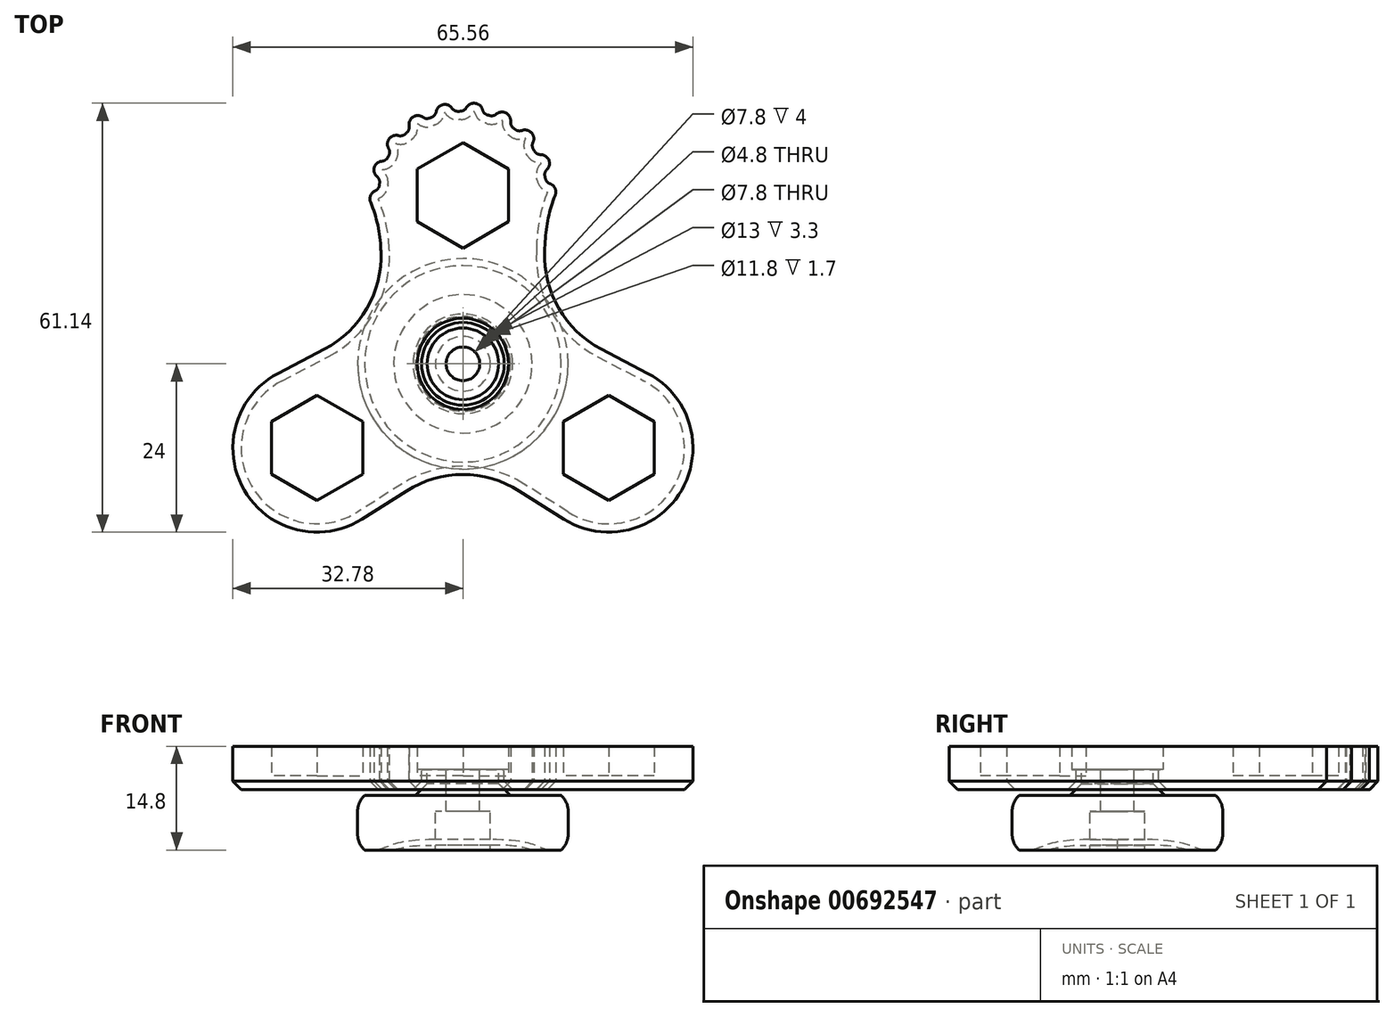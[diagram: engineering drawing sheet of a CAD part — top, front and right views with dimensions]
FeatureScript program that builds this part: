
annotation { "Feature Type Name" : "Feature", "Feature Type Description" : "" }
export const myFeature = defineFeature(function(context is Context, id is Id, definition is map)
    precondition{}
    {
        {
            var Q0;
            Q0=qCreatedBy(makeId("Top.planeOp"),FACE);
            var sketch = newSketch(context, id + "F0", { "sketchPlane" : qUnion([Q0])});
            skCircle(sketch, "E0", {"center": v(0, 0) * mm, "radius": 6.5 * mm});
            skCircle(sketch, "E1.cCircle", {"center": v(0, 24) * mm, "radius": 6.5 * mm, "construction": true});
            skLineSegment(sketch, "E1.0", {"start": v(6.5, 27.75) * mm, "end": v(6.5, 20.25) * mm});
            skLineSegment(sketch, "E1.1", {"start": v(6.5, 20.25) * mm, "end": v(0, 16.5) * mm});
            skLineSegment(sketch, "E1.2", {"start": v(0, 16.5) * mm, "end": v(-6.5, 20.25) * mm});
            skLineSegment(sketch, "E1.3", {"start": v(-6.5, 20.25) * mm, "end": v(-6.5, 27.75) * mm});
            skLineSegment(sketch, "E1.4", {"start": v(-6.5, 27.75) * mm, "end": v(0, 31.5) * mm});
            skLineSegment(sketch, "E1.5", {"start": v(0, 31.5) * mm, "end": v(6.5, 27.75) * mm});
            skPoint(sketch, "E1.0.midPoint", {"position": v(6.5, 24) * mm});
            skCircle(sketch, "E2", {"center": v(0, 24) * mm, "radius": 12 * mm});
            skCircle(sketch, "E3", {"center": v(0, 0) * mm, "radius": 11 * mm});
            skLineSegment(sketch, "E4", {"start": v(-11.99, 23.5) * mm, "end": v(-11, -0.46) * mm});
            skLineSegment(sketch, "E5", {"start": v(11.99, 23.5) * mm, "end": v(11, -0.46) * mm});
            skCircle(sketch, "E6.1.0", {"center": v(-20.78, -12) * mm, "radius": 12 * mm});
            skLineSegment(sketch, "E6.1.1", {"start": v(-27.28, -15.75) * mm, "end": v(-27.28, -8.25) * mm});
            skLineSegment(sketch, "E6.1.2", {"start": v(-27.28, -8.25) * mm, "end": v(-20.78, -4.5) * mm});
            skLineSegment(sketch, "E6.1.3", {"start": v(-20.78, -4.5) * mm, "end": v(-14.28, -8.25) * mm});
            skLineSegment(sketch, "E6.1.4", {"start": v(-14.28, -8.25) * mm, "end": v(-14.28, -15.75) * mm});
            skLineSegment(sketch, "E6.1.5", {"start": v(-14.28, -15.75) * mm, "end": v(-20.78, -19.5) * mm});
            skLineSegment(sketch, "E6.1.6", {"start": v(-20.78, -19.5) * mm, "end": v(-27.28, -15.75) * mm});
            skLineSegment(sketch, "E6.1.7", {"start": v(-14.36, -22.13) * mm, "end": v(5.9, -9.29) * mm});
            skLineSegment(sketch, "E6.1.8", {"start": v(-26.35, -1.37) * mm, "end": v(-5.1, 9.75) * mm});
            skCircle(sketch, "E6.2.0", {"center": v(20.78, -12) * mm, "radius": 12 * mm});
            skLineSegment(sketch, "E6.2.1", {"start": v(27.28, -15.75) * mm, "end": v(20.78, -19.5) * mm});
            skLineSegment(sketch, "E6.2.2", {"start": v(20.78, -19.5) * mm, "end": v(14.28, -15.75) * mm});
            skLineSegment(sketch, "E6.2.3", {"start": v(14.28, -15.75) * mm, "end": v(14.28, -8.25) * mm});
            skLineSegment(sketch, "E6.2.4", {"start": v(14.28, -8.25) * mm, "end": v(20.78, -4.5) * mm});
            skLineSegment(sketch, "E6.2.5", {"start": v(20.78, -4.5) * mm, "end": v(27.28, -8.25) * mm});
            skLineSegment(sketch, "E6.2.6", {"start": v(27.28, -8.25) * mm, "end": v(27.28, -15.75) * mm});
            skLineSegment(sketch, "E6.2.7", {"start": v(26.35, -1.37) * mm, "end": v(5.1, 9.75) * mm});
            skLineSegment(sketch, "E6.2.8", {"start": v(14.36, -22.13) * mm, "end": v(-5.9, -9.29) * mm});
            skSolve(sketch);
        }
        {
            var Q0;
            Q0 = qSketchRegion(id + "F0", true);
            var Q1;
            Q1=makeQuery(id+"F0.imprint","IMPRINT",FACE,{"disambiguationData":[TD([[makeQuery(id+"F0.imprint","IMPRINT",EDGE,{"derivedFrom":sQuery(id+"F0.wireOp",EDGE,"E0")}),-1.0]])]});
            extrude(context, id + "F1", {"entities" : qUnion([Q0, Q1]), "depth" : 4.2 * mm, "offsetDistance" : 25 * mm});
        }
        {
            var Q0;
            Q0=makeQuery(id+"F1.opExtrude","CAP_FACE",FACE,{"disambiguationData":[OSD([sQuery(id+"F0.wireOp",EDGE,"E0"),sQuery(id+"F0.wireOp",EDGE,"E1.0"),sQuery(id+"F0.wireOp",EDGE,"E1.1"),sQuery(id+"F0.wireOp",EDGE,"E1.2"),sQuery(id+"F0.wireOp",EDGE,"E1.3"),sQuery(id+"F0.wireOp",EDGE,"E1.4"),sQuery(id+"F0.wireOp",EDGE,"E1.5"),sQuery(id+"F0.wireOp",EDGE,"E2"),sQuery(id+"F0.wireOp",EDGE,"E4"),sQuery(id+"F0.wireOp",EDGE,"E5"),sQuery(id+"F0.wireOp",EDGE,"E6.1.0"),sQuery(id+"F0.wireOp",EDGE,"E6.1.1"),sQuery(id+"F0.wireOp",EDGE,"E6.1.2"),sQuery(id+"F0.wireOp",EDGE,"E6.1.3"),sQuery(id+"F0.wireOp",EDGE,"E6.1.4"),sQuery(id+"F0.wireOp",EDGE,"E6.1.5"),sQuery(id+"F0.wireOp",EDGE,"E6.1.6"),sQuery(id+"F0.wireOp",EDGE,"E6.1.7"),sQuery(id+"F0.wireOp",EDGE,"E6.1.8"),sQuery(id+"F0.wireOp",EDGE,"E6.2.0"),sQuery(id+"F0.wireOp",EDGE,"E6.2.1"),sQuery(id+"F0.wireOp",EDGE,"E6.2.2"),sQuery(id+"F0.wireOp",EDGE,"E6.2.3"),sQuery(id+"F0.wireOp",EDGE,"E6.2.4"),sQuery(id+"F0.wireOp",EDGE,"E6.2.5"),sQuery(id+"F0.wireOp",EDGE,"E6.2.6"),sQuery(id+"F0.wireOp",EDGE,"E6.2.7"),sQuery(id+"F0.wireOp",EDGE,"E6.2.8")])],"isStart":true});
            var sketch = newSketch(context, id + "F2", { "sketchPlane" : qUnion([Q0])});
            skCircle(sketch, "E7", {"center": v(0, 0) * mm, "radius": 5.9 * mm});
            skSolve(sketch);
        }
        {
            var Q0;
            Q0=makeQuery(id+"F2.imprint","IMPRINT",FACE,{"disambiguationData":[TD([[makeQuery(id+"F2.imprint","IMPRINT",EDGE,{"derivedFrom":makeQuery(id+"F1.opExtrude","CAP_EDGE",EDGE,{"disambiguationData":[OSD([sQuery(id+"F0.wireOp",EDGE,"E1.0")])],"isStart":true})}),1.0]])]});
            var Q1;
            Q1=makeQuery(id+"F2.imprint","IMPRINT",FACE,{"disambiguationData":[TD([[makeQuery(id+"F2.imprint","IMPRINT",EDGE,{"derivedFrom":makeQuery(id+"F1.opExtrude","CAP_EDGE",EDGE,{"disambiguationData":[OSD([sQuery(id+"F0.wireOp",EDGE,"E0")])],"isStart":true})}),1.0]])]});
            var Q2;
            Q2=makeQuery(id+"F2.imprint","IMPRINT",FACE,{"disambiguationData":[TD([[makeQuery(id+"F2.imprint","IMPRINT",EDGE,{"derivedFrom":makeQuery(id+"F1.opExtrude","CAP_EDGE",EDGE,{"disambiguationData":[OSD([sQuery(id+"F0.wireOp",EDGE,"E0")])],"isStart":true})}),-1.0]])]});
            var Q3;
            Q3=makeQuery(id+"F2.imprint","IMPRINT",FACE,{"disambiguationData":[TD([[makeQuery(id+"F2.imprint","IMPRINT",EDGE,{"derivedFrom":makeQuery(id+"F1.opExtrude","CAP_EDGE",EDGE,{"disambiguationData":[OSD([sQuery(id+"F0.wireOp",EDGE,"E6.2.1")])],"isStart":true})}),1.0]])]});
            var Q4;
            Q4=makeQuery(id+"F2.imprint","IMPRINT",FACE,{"disambiguationData":[TD([[makeQuery(id+"F2.imprint","IMPRINT",EDGE,{"derivedFrom":makeQuery(id+"F1.opExtrude","CAP_EDGE",EDGE,{"disambiguationData":[OSD([sQuery(id+"F0.wireOp",EDGE,"E6.1.1")])],"isStart":true})}),1.0]])]});
            extrude(context, id + "F3", {"entities" : qUnion([Q0, Q1, Q2, Q3, Q4]), "operationType" : NewBodyOperationType.ADD, "depth" : 2 * mm, "offsetDistance" : 25 * mm});
        }
        {
            var Q0;
            {var subQ0=sQuery(id+"F2.wireOp",EDGE,"E7");Q0=makeQuery(id+"F3.boolean.opBoolean","SPLIT",FACE,{"disambiguationData":[TD([makeQuery(id+"F1.opExtrude","SWEPT_FACE",FACE,{"disambiguationData":[OSD([sQuery(id+"F0.wireOp",EDGE,"E0")])]})])],"derivedFrom":makeQuery(id+"F3.opExtrude","CAP_FACE",FACE,{"disambiguationData":[OSD([sQuery(id+"F0.wireOp",EDGE,"E2"),sQuery(id+"F0.wireOp",EDGE,"E4"),sQuery(id+"F0.wireOp",EDGE,"E5"),sQuery(id+"F0.wireOp",EDGE,"E6.1.0"),sQuery(id+"F0.wireOp",EDGE,"E6.1.7"),sQuery(id+"F0.wireOp",EDGE,"E6.1.8"),sQuery(id+"F0.wireOp",EDGE,"E6.2.0"),sQuery(id+"F0.wireOp",EDGE,"E6.2.7"),sQuery(id+"F0.wireOp",EDGE,"E6.2.8"),subQ0])],"isStart":true})});}
            extrude(context, id + "F4", {"entities" : qUnion([Q0]), "operationType" : NewBodyOperationType.ADD, "depth" : .9 * mm, "offsetDistance" : 25 * mm});
        }
        {
            var Q0;
            {var subQ0=sQuery(id+"F0.wireOp",EDGE,"E6.1.8");var subQ1=sQuery(id+"F0.wireOp",EDGE,"E4");Q0=makeQuery(id+"F3.boolean.opBoolean","MERGE",EDGE,{"derivedFrom":[makeQuery(id+"F1.opExtrude","SWEPT_EDGE",EDGE,{"disambiguationData":[OSD([subQ1,subQ0])]}),makeQuery(id+"F3.opExtrude","SWEPT_EDGE",EDGE,{"disambiguationData":[OSD([subQ1,subQ0])]})]});}
            var Q1;
            {var subQ0=sQuery(id+"F0.wireOp",EDGE,"E6.2.7");var subQ1=sQuery(id+"F0.wireOp",EDGE,"E5");Q1=makeQuery(id+"F3.boolean.opBoolean","MERGE",EDGE,{"derivedFrom":[makeQuery(id+"F1.opExtrude","SWEPT_EDGE",EDGE,{"disambiguationData":[OSD([subQ1,subQ0])]}),makeQuery(id+"F3.opExtrude","SWEPT_EDGE",EDGE,{"disambiguationData":[OSD([subQ1,subQ0])]})]});}
            var Q2;
            {var subQ0=sQuery(id+"F0.wireOp",EDGE,"E6.2.8");var subQ1=sQuery(id+"F0.wireOp",EDGE,"E6.1.7");Q2=makeQuery(id+"F3.boolean.opBoolean","MERGE",EDGE,{"derivedFrom":[makeQuery(id+"F1.opExtrude","SWEPT_EDGE",EDGE,{"disambiguationData":[OSD([subQ1,subQ0])]}),makeQuery(id+"F3.opExtrude","SWEPT_EDGE",EDGE,{"disambiguationData":[OSD([subQ1,subQ0])]})]});}
            fillet(context, id + "F5", {"entities" : qUnion([Q0, Q1, Q2]), "radius" : 15 * mm, "tangentPropagation" : true, "allowEdgeOverflow" : false});
        }
        {
            var Q0;
            Q0=makeQuery(id+"F3.opExtrude","CAP_FACE",FACE,{"disambiguationData":[OSD([sQuery(id+"F0.wireOp",EDGE,"E2"),sQuery(id+"F0.wireOp",EDGE,"E4"),sQuery(id+"F0.wireOp",EDGE,"E5"),sQuery(id+"F0.wireOp",EDGE,"E6.1.0"),sQuery(id+"F0.wireOp",EDGE,"E6.1.7"),sQuery(id+"F0.wireOp",EDGE,"E6.1.8"),sQuery(id+"F0.wireOp",EDGE,"E6.2.0"),sQuery(id+"F0.wireOp",EDGE,"E6.2.7"),sQuery(id+"F0.wireOp",EDGE,"E6.2.8"),sQuery(id+"F2.wireOp",EDGE,"E7")])],"isStart":false});
            var sketch = newSketch(context, id + "F6", { "sketchPlane" : qUnion([Q0])});
            skCircle(sketch, "E8", {"center": v(-11.99, -23.5) * mm, "radius": 1.25 * mm});
            skCircle(sketch, "E9.1.0", {"center": v(-11.44, -27.63) * mm, "radius": 1.25 * mm});
            skCircle(sketch, "E9.2.0", {"center": v(-9.5, -31.32) * mm, "radius": 1.25 * mm});
            skCircle(sketch, "E9.3.0", {"center": v(-6.43, -34.13) * mm, "radius": 1.25 * mm});
            skCircle(sketch, "E9.4.0", {"center": v(-2.57, -35.72) * mm, "radius": 1.25 * mm});
            skCircle(sketch, "E9.5.0", {"center": v(1.59, -35.9) * mm, "radius": 1.25 * mm});
            skPoint(sketch, "E9.center", {"position": v(0, -24) * mm});
            skLineSegment(sketch, "E9.anchor1", {"start": v(0, -24) * mm, "end": v(-11.99, -23.5) * mm, "construction": true});
            skLineSegment(sketch, "E9.anchor2", {"start": v(0, -24) * mm, "end": v(11.99, -24.5) * mm, "construction": true});
            skCircle(sketch, "E10.1.6.0", {"center": v(5.56, -34.63) * mm, "radius": 1.25 * mm});
            skCircle(sketch, "E10.1.7.0", {"center": v(8.86, -32.09) * mm, "radius": 1.25 * mm});
            skCircle(sketch, "E10.1.8.0", {"center": v(11.1, -28.57) * mm, "radius": 1.25 * mm});
            skCircle(sketch, "E10.1.9.0", {"center": v(11.99, -24.5) * mm, "radius": 1.25 * mm});
            skSolve(sketch);
        }
        {
            var Q0;
            Q0 = qSketchRegion(id + "F6", true);
            var Q1;
            Q1=makeQuery(id+"F1.opExtrude","CAP_FACE",FACE,{"disambiguationData":[OSD([sQuery(id+"F0.wireOp",EDGE,"E0"),sQuery(id+"F0.wireOp",EDGE,"E1.0"),sQuery(id+"F0.wireOp",EDGE,"E1.1"),sQuery(id+"F0.wireOp",EDGE,"E1.2"),sQuery(id+"F0.wireOp",EDGE,"E1.3"),sQuery(id+"F0.wireOp",EDGE,"E1.4"),sQuery(id+"F0.wireOp",EDGE,"E1.5"),sQuery(id+"F0.wireOp",EDGE,"E2"),sQuery(id+"F0.wireOp",EDGE,"E4"),sQuery(id+"F0.wireOp",EDGE,"E5"),sQuery(id+"F0.wireOp",EDGE,"E6.1.0"),sQuery(id+"F0.wireOp",EDGE,"E6.1.1"),sQuery(id+"F0.wireOp",EDGE,"E6.1.2"),sQuery(id+"F0.wireOp",EDGE,"E6.1.3"),sQuery(id+"F0.wireOp",EDGE,"E6.1.4"),sQuery(id+"F0.wireOp",EDGE,"E6.1.5"),sQuery(id+"F0.wireOp",EDGE,"E6.1.6"),sQuery(id+"F0.wireOp",EDGE,"E6.1.7"),sQuery(id+"F0.wireOp",EDGE,"E6.1.8"),sQuery(id+"F0.wireOp",EDGE,"E6.2.0"),sQuery(id+"F0.wireOp",EDGE,"E6.2.1"),sQuery(id+"F0.wireOp",EDGE,"E6.2.2"),sQuery(id+"F0.wireOp",EDGE,"E6.2.3"),sQuery(id+"F0.wireOp",EDGE,"E6.2.4"),sQuery(id+"F0.wireOp",EDGE,"E6.2.5"),sQuery(id+"F0.wireOp",EDGE,"E6.2.6"),sQuery(id+"F0.wireOp",EDGE,"E6.2.7"),sQuery(id+"F0.wireOp",EDGE,"E6.2.8")])],"isStart":false});
            extrude(context, id + "F7", {"entities" : qUnion([Q0]), "operationType" : NewBodyOperationType.ADD, "endBound" : BoundingType.UP_TO_SURFACE, "oppositeDirection" : true, "depth" : 25 * mm, "endBoundEntityFace" : qUnion([Q1]), "offsetDistance" : 25 * mm});
        }
        {
            var Q0;
            {var subQ0=sQuery(id+"F0.wireOp",EDGE,"E2");Q0=makeQuery(id+"F7.boolean.opBoolean","INTERSECT",EDGE,{"disambiguationData":[OD(0.0)],"derivedFrom":[makeQuery(id+"F3.boolean.opBoolean","MERGE",FACE,{"derivedFrom":[makeQuery(id+"F1.opExtrude","SWEPT_FACE",FACE,{"disambiguationData":[OSD([subQ0])]}),makeQuery(id+"F3.opExtrude","SWEPT_FACE",FACE,{"disambiguationData":[OSD([subQ0])]})]}),makeQuery(id+"F7.opExtrude","SWEPT_FACE",FACE,{"disambiguationData":[OSD([sQuery(id+"F6.wireOp",EDGE,"E9.5.0")])]})]});}
            var Q1;
            {var subQ0=sQuery(id+"F0.wireOp",EDGE,"E2");Q1=makeQuery(id+"F7.boolean.opBoolean","INTERSECT",EDGE,{"disambiguationData":[OD(1.0)],"derivedFrom":[makeQuery(id+"F3.boolean.opBoolean","MERGE",FACE,{"derivedFrom":[makeQuery(id+"F1.opExtrude","SWEPT_FACE",FACE,{"disambiguationData":[OSD([subQ0])]}),makeQuery(id+"F3.opExtrude","SWEPT_FACE",FACE,{"disambiguationData":[OSD([subQ0])]})]}),makeQuery(id+"F7.opExtrude","SWEPT_FACE",FACE,{"disambiguationData":[OSD([sQuery(id+"F6.wireOp",EDGE,"E9.5.0")])]})]});}
            var Q2;
            {var subQ0=sQuery(id+"F0.wireOp",EDGE,"E2");Q2=makeQuery(id+"F7.boolean.opBoolean","INTERSECT",EDGE,{"derivedFrom":[makeQuery(id+"F3.boolean.opBoolean","MERGE",FACE,{"derivedFrom":[makeQuery(id+"F1.opExtrude","SWEPT_FACE",FACE,{"disambiguationData":[OSD([subQ0])]}),makeQuery(id+"F3.opExtrude","SWEPT_FACE",FACE,{"disambiguationData":[OSD([subQ0])]})]}),makeQuery(id+"F7.opExtrude","SWEPT_FACE",FACE,{"disambiguationData":[OSD([sQuery(id+"F6.wireOp",EDGE,"E8")])]})]});}
            var Q3;
            {var subQ0=sQuery(id+"F0.wireOp",EDGE,"E2");Q3=makeQuery(id+"F7.boolean.opBoolean","INTERSECT",EDGE,{"disambiguationData":[OD(0.0)],"derivedFrom":[makeQuery(id+"F3.boolean.opBoolean","MERGE",FACE,{"derivedFrom":[makeQuery(id+"F1.opExtrude","SWEPT_FACE",FACE,{"disambiguationData":[OSD([subQ0])]}),makeQuery(id+"F3.opExtrude","SWEPT_FACE",FACE,{"disambiguationData":[OSD([subQ0])]})]}),makeQuery(id+"F7.opExtrude","SWEPT_FACE",FACE,{"disambiguationData":[OSD([sQuery(id+"F6.wireOp",EDGE,"E9.1.0")])]})]});}
            var Q4;
            {var subQ0=sQuery(id+"F0.wireOp",EDGE,"E2");Q4=makeQuery(id+"F7.boolean.opBoolean","INTERSECT",EDGE,{"disambiguationData":[OD(1.0)],"derivedFrom":[makeQuery(id+"F3.boolean.opBoolean","MERGE",FACE,{"derivedFrom":[makeQuery(id+"F1.opExtrude","SWEPT_FACE",FACE,{"disambiguationData":[OSD([subQ0])]}),makeQuery(id+"F3.opExtrude","SWEPT_FACE",FACE,{"disambiguationData":[OSD([subQ0])]})]}),makeQuery(id+"F7.opExtrude","SWEPT_FACE",FACE,{"disambiguationData":[OSD([sQuery(id+"F6.wireOp",EDGE,"E9.1.0")])]})]});}
            var Q5;
            {var subQ0=sQuery(id+"F0.wireOp",EDGE,"E2");Q5=makeQuery(id+"F7.boolean.opBoolean","INTERSECT",EDGE,{"disambiguationData":[OD(0.0)],"derivedFrom":[makeQuery(id+"F3.boolean.opBoolean","MERGE",FACE,{"derivedFrom":[makeQuery(id+"F1.opExtrude","SWEPT_FACE",FACE,{"disambiguationData":[OSD([subQ0])]}),makeQuery(id+"F3.opExtrude","SWEPT_FACE",FACE,{"disambiguationData":[OSD([subQ0])]})]}),makeQuery(id+"F7.opExtrude","SWEPT_FACE",FACE,{"disambiguationData":[OSD([sQuery(id+"F6.wireOp",EDGE,"E9.2.0")])]})]});}
            var Q6;
            {var subQ0=sQuery(id+"F0.wireOp",EDGE,"E2");Q6=makeQuery(id+"F7.boolean.opBoolean","INTERSECT",EDGE,{"disambiguationData":[OD(1.0)],"derivedFrom":[makeQuery(id+"F3.boolean.opBoolean","MERGE",FACE,{"derivedFrom":[makeQuery(id+"F1.opExtrude","SWEPT_FACE",FACE,{"disambiguationData":[OSD([subQ0])]}),makeQuery(id+"F3.opExtrude","SWEPT_FACE",FACE,{"disambiguationData":[OSD([subQ0])]})]}),makeQuery(id+"F7.opExtrude","SWEPT_FACE",FACE,{"disambiguationData":[OSD([sQuery(id+"F6.wireOp",EDGE,"E9.2.0")])]})]});}
            var Q7;
            {var subQ0=sQuery(id+"F0.wireOp",EDGE,"E2");Q7=makeQuery(id+"F7.boolean.opBoolean","INTERSECT",EDGE,{"disambiguationData":[OD(0.0)],"derivedFrom":[makeQuery(id+"F3.boolean.opBoolean","MERGE",FACE,{"derivedFrom":[makeQuery(id+"F1.opExtrude","SWEPT_FACE",FACE,{"disambiguationData":[OSD([subQ0])]}),makeQuery(id+"F3.opExtrude","SWEPT_FACE",FACE,{"disambiguationData":[OSD([subQ0])]})]}),makeQuery(id+"F7.opExtrude","SWEPT_FACE",FACE,{"disambiguationData":[OSD([sQuery(id+"F6.wireOp",EDGE,"E9.3.0")])]})]});}
            var Q8;
            {var subQ0=sQuery(id+"F0.wireOp",EDGE,"E2");Q8=makeQuery(id+"F7.boolean.opBoolean","INTERSECT",EDGE,{"disambiguationData":[OD(1.0)],"derivedFrom":[makeQuery(id+"F3.boolean.opBoolean","MERGE",FACE,{"derivedFrom":[makeQuery(id+"F1.opExtrude","SWEPT_FACE",FACE,{"disambiguationData":[OSD([subQ0])]}),makeQuery(id+"F3.opExtrude","SWEPT_FACE",FACE,{"disambiguationData":[OSD([subQ0])]})]}),makeQuery(id+"F7.opExtrude","SWEPT_FACE",FACE,{"disambiguationData":[OSD([sQuery(id+"F6.wireOp",EDGE,"E9.3.0")])]})]});}
            var Q9;
            {var subQ0=sQuery(id+"F0.wireOp",EDGE,"E2");Q9=makeQuery(id+"F7.boolean.opBoolean","INTERSECT",EDGE,{"disambiguationData":[OD(0.0)],"derivedFrom":[makeQuery(id+"F3.boolean.opBoolean","MERGE",FACE,{"derivedFrom":[makeQuery(id+"F1.opExtrude","SWEPT_FACE",FACE,{"disambiguationData":[OSD([subQ0])]}),makeQuery(id+"F3.opExtrude","SWEPT_FACE",FACE,{"disambiguationData":[OSD([subQ0])]})]}),makeQuery(id+"F7.opExtrude","SWEPT_FACE",FACE,{"disambiguationData":[OSD([sQuery(id+"F6.wireOp",EDGE,"E9.4.0")])]})]});}
            var Q10;
            {var subQ0=sQuery(id+"F0.wireOp",EDGE,"E2");Q10=makeQuery(id+"F7.boolean.opBoolean","INTERSECT",EDGE,{"disambiguationData":[OD(1.0)],"derivedFrom":[makeQuery(id+"F3.boolean.opBoolean","MERGE",FACE,{"derivedFrom":[makeQuery(id+"F1.opExtrude","SWEPT_FACE",FACE,{"disambiguationData":[OSD([subQ0])]}),makeQuery(id+"F3.opExtrude","SWEPT_FACE",FACE,{"disambiguationData":[OSD([subQ0])]})]}),makeQuery(id+"F7.opExtrude","SWEPT_FACE",FACE,{"disambiguationData":[OSD([sQuery(id+"F6.wireOp",EDGE,"E9.4.0")])]})]});}
            var Q11;
            {var subQ0=sQuery(id+"F0.wireOp",EDGE,"E2");Q11=makeQuery(id+"F7.boolean.opBoolean","INTERSECT",EDGE,{"derivedFrom":[makeQuery(id+"F3.boolean.opBoolean","MERGE",FACE,{"derivedFrom":[makeQuery(id+"F1.opExtrude","SWEPT_FACE",FACE,{"disambiguationData":[OSD([subQ0])]}),makeQuery(id+"F3.opExtrude","SWEPT_FACE",FACE,{"disambiguationData":[OSD([subQ0])]})]}),makeQuery(id+"F7.opExtrude","SWEPT_FACE",FACE,{"disambiguationData":[OSD([sQuery(id+"F6.wireOp",EDGE,"E10.1.9.0")])]})]});}
            var Q12;
            {var subQ0=sQuery(id+"F0.wireOp",EDGE,"E2");Q12=makeQuery(id+"F7.boolean.opBoolean","INTERSECT",EDGE,{"disambiguationData":[OD(1.0)],"derivedFrom":[makeQuery(id+"F3.boolean.opBoolean","MERGE",FACE,{"derivedFrom":[makeQuery(id+"F1.opExtrude","SWEPT_FACE",FACE,{"disambiguationData":[OSD([subQ0])]}),makeQuery(id+"F3.opExtrude","SWEPT_FACE",FACE,{"disambiguationData":[OSD([subQ0])]})]}),makeQuery(id+"F7.opExtrude","SWEPT_FACE",FACE,{"disambiguationData":[OSD([sQuery(id+"F6.wireOp",EDGE,"E10.1.8.0")])]})]});}
            var Q13;
            {var subQ0=sQuery(id+"F0.wireOp",EDGE,"E2");Q13=makeQuery(id+"F7.boolean.opBoolean","INTERSECT",EDGE,{"disambiguationData":[OD(0.0)],"derivedFrom":[makeQuery(id+"F3.boolean.opBoolean","MERGE",FACE,{"derivedFrom":[makeQuery(id+"F1.opExtrude","SWEPT_FACE",FACE,{"disambiguationData":[OSD([subQ0])]}),makeQuery(id+"F3.opExtrude","SWEPT_FACE",FACE,{"disambiguationData":[OSD([subQ0])]})]}),makeQuery(id+"F7.opExtrude","SWEPT_FACE",FACE,{"disambiguationData":[OSD([sQuery(id+"F6.wireOp",EDGE,"E10.1.8.0")])]})]});}
            var Q14;
            {var subQ0=sQuery(id+"F0.wireOp",EDGE,"E2");Q14=makeQuery(id+"F7.boolean.opBoolean","INTERSECT",EDGE,{"disambiguationData":[OD(1.0)],"derivedFrom":[makeQuery(id+"F3.boolean.opBoolean","MERGE",FACE,{"derivedFrom":[makeQuery(id+"F1.opExtrude","SWEPT_FACE",FACE,{"disambiguationData":[OSD([subQ0])]}),makeQuery(id+"F3.opExtrude","SWEPT_FACE",FACE,{"disambiguationData":[OSD([subQ0])]})]}),makeQuery(id+"F7.opExtrude","SWEPT_FACE",FACE,{"disambiguationData":[OSD([sQuery(id+"F6.wireOp",EDGE,"E10.1.7.0")])]})]});}
            var Q15;
            {var subQ0=sQuery(id+"F0.wireOp",EDGE,"E2");Q15=makeQuery(id+"F7.boolean.opBoolean","INTERSECT",EDGE,{"disambiguationData":[OD(0.0)],"derivedFrom":[makeQuery(id+"F3.boolean.opBoolean","MERGE",FACE,{"derivedFrom":[makeQuery(id+"F1.opExtrude","SWEPT_FACE",FACE,{"disambiguationData":[OSD([subQ0])]}),makeQuery(id+"F3.opExtrude","SWEPT_FACE",FACE,{"disambiguationData":[OSD([subQ0])]})]}),makeQuery(id+"F7.opExtrude","SWEPT_FACE",FACE,{"disambiguationData":[OSD([sQuery(id+"F6.wireOp",EDGE,"E10.1.7.0")])]})]});}
            var Q16;
            {var subQ0=sQuery(id+"F0.wireOp",EDGE,"E2");Q16=makeQuery(id+"F7.boolean.opBoolean","INTERSECT",EDGE,{"disambiguationData":[OD(1.0)],"derivedFrom":[makeQuery(id+"F3.boolean.opBoolean","MERGE",FACE,{"derivedFrom":[makeQuery(id+"F1.opExtrude","SWEPT_FACE",FACE,{"disambiguationData":[OSD([subQ0])]}),makeQuery(id+"F3.opExtrude","SWEPT_FACE",FACE,{"disambiguationData":[OSD([subQ0])]})]}),makeQuery(id+"F7.opExtrude","SWEPT_FACE",FACE,{"disambiguationData":[OSD([sQuery(id+"F6.wireOp",EDGE,"E10.1.6.0")])]})]});}
            var Q17;
            {var subQ0=sQuery(id+"F0.wireOp",EDGE,"E2");Q17=makeQuery(id+"F7.boolean.opBoolean","INTERSECT",EDGE,{"disambiguationData":[OD(0.0)],"derivedFrom":[makeQuery(id+"F3.boolean.opBoolean","MERGE",FACE,{"derivedFrom":[makeQuery(id+"F1.opExtrude","SWEPT_FACE",FACE,{"disambiguationData":[OSD([subQ0])]}),makeQuery(id+"F3.opExtrude","SWEPT_FACE",FACE,{"disambiguationData":[OSD([subQ0])]})]}),makeQuery(id+"F7.opExtrude","SWEPT_FACE",FACE,{"disambiguationData":[OSD([sQuery(id+"F6.wireOp",EDGE,"E10.1.6.0")])]})]});}
            var Q18;
            {var subQ0=sQuery(id+"F0.wireOp",EDGE,"E6.1.0");Q18=makeQuery(id+"FehnNMLxcj5brBZ_1.2.F7.boolean.opBoolean","INTERSECT",EDGE,{"derivedFrom":[makeQuery(id+"F3.boolean.opBoolean","MERGE",FACE,{"derivedFrom":[makeQuery(id+"F1.opExtrude","SWEPT_FACE",FACE,{"disambiguationData":[OSD([subQ0])]}),makeQuery(id+"F3.opExtrude","SWEPT_FACE",FACE,{"disambiguationData":[OSD([subQ0])]})]}),makeQuery(id+"FehnNMLxcj5brBZ_1.2.F7.opExtrude","SWEPT_FACE",FACE,{"disambiguationData":[OSD([sQuery(id+"F6.wireOp",EDGE,"E10.1.9.0")])]})]});}
            var Q19;
            {var subQ0=sQuery(id+"F0.wireOp",EDGE,"E6.1.0");Q19=makeQuery(id+"FehnNMLxcj5brBZ_1.2.F7.boolean.opBoolean","INTERSECT",EDGE,{"disambiguationData":[OD(1.0)],"derivedFrom":[makeQuery(id+"F3.boolean.opBoolean","MERGE",FACE,{"derivedFrom":[makeQuery(id+"F1.opExtrude","SWEPT_FACE",FACE,{"disambiguationData":[OSD([subQ0])]}),makeQuery(id+"F3.opExtrude","SWEPT_FACE",FACE,{"disambiguationData":[OSD([subQ0])]})]}),makeQuery(id+"FehnNMLxcj5brBZ_1.2.F7.opExtrude","SWEPT_FACE",FACE,{"disambiguationData":[OSD([sQuery(id+"F6.wireOp",EDGE,"E10.1.8.0")])]})]});}
            var Q20;
            {var subQ0=sQuery(id+"F0.wireOp",EDGE,"E6.1.0");Q20=makeQuery(id+"FehnNMLxcj5brBZ_1.2.F7.boolean.opBoolean","INTERSECT",EDGE,{"disambiguationData":[OD(0.0)],"derivedFrom":[makeQuery(id+"F3.boolean.opBoolean","MERGE",FACE,{"derivedFrom":[makeQuery(id+"F1.opExtrude","SWEPT_FACE",FACE,{"disambiguationData":[OSD([subQ0])]}),makeQuery(id+"F3.opExtrude","SWEPT_FACE",FACE,{"disambiguationData":[OSD([subQ0])]})]}),makeQuery(id+"FehnNMLxcj5brBZ_1.2.F7.opExtrude","SWEPT_FACE",FACE,{"disambiguationData":[OSD([sQuery(id+"F6.wireOp",EDGE,"E10.1.8.0")])]})]});}
            var Q21;
            {var subQ0=sQuery(id+"F0.wireOp",EDGE,"E6.1.0");Q21=makeQuery(id+"FehnNMLxcj5brBZ_1.2.F7.boolean.opBoolean","INTERSECT",EDGE,{"disambiguationData":[OD(1.0)],"derivedFrom":[makeQuery(id+"F3.boolean.opBoolean","MERGE",FACE,{"derivedFrom":[makeQuery(id+"F1.opExtrude","SWEPT_FACE",FACE,{"disambiguationData":[OSD([subQ0])]}),makeQuery(id+"F3.opExtrude","SWEPT_FACE",FACE,{"disambiguationData":[OSD([subQ0])]})]}),makeQuery(id+"FehnNMLxcj5brBZ_1.2.F7.opExtrude","SWEPT_FACE",FACE,{"disambiguationData":[OSD([sQuery(id+"F6.wireOp",EDGE,"E10.1.7.0")])]})]});}
            var Q22;
            {var subQ0=sQuery(id+"F0.wireOp",EDGE,"E6.1.0");Q22=makeQuery(id+"FehnNMLxcj5brBZ_1.2.F7.boolean.opBoolean","INTERSECT",EDGE,{"disambiguationData":[OD(0.0)],"derivedFrom":[makeQuery(id+"F3.boolean.opBoolean","MERGE",FACE,{"derivedFrom":[makeQuery(id+"F1.opExtrude","SWEPT_FACE",FACE,{"disambiguationData":[OSD([subQ0])]}),makeQuery(id+"F3.opExtrude","SWEPT_FACE",FACE,{"disambiguationData":[OSD([subQ0])]})]}),makeQuery(id+"FehnNMLxcj5brBZ_1.2.F7.opExtrude","SWEPT_FACE",FACE,{"disambiguationData":[OSD([sQuery(id+"F6.wireOp",EDGE,"E10.1.7.0")])]})]});}
            var Q23;
            {var subQ0=sQuery(id+"F0.wireOp",EDGE,"E6.1.0");Q23=makeQuery(id+"FehnNMLxcj5brBZ_1.2.F7.boolean.opBoolean","INTERSECT",EDGE,{"disambiguationData":[OD(1.0)],"derivedFrom":[makeQuery(id+"F3.boolean.opBoolean","MERGE",FACE,{"derivedFrom":[makeQuery(id+"F1.opExtrude","SWEPT_FACE",FACE,{"disambiguationData":[OSD([subQ0])]}),makeQuery(id+"F3.opExtrude","SWEPT_FACE",FACE,{"disambiguationData":[OSD([subQ0])]})]}),makeQuery(id+"FehnNMLxcj5brBZ_1.2.F7.opExtrude","SWEPT_FACE",FACE,{"disambiguationData":[OSD([sQuery(id+"F6.wireOp",EDGE,"E10.1.6.0")])]})]});}
            var Q24;
            {var subQ0=sQuery(id+"F0.wireOp",EDGE,"E6.1.0");Q24=makeQuery(id+"FehnNMLxcj5brBZ_1.2.F7.boolean.opBoolean","INTERSECT",EDGE,{"disambiguationData":[OD(0.0)],"derivedFrom":[makeQuery(id+"F3.boolean.opBoolean","MERGE",FACE,{"derivedFrom":[makeQuery(id+"F1.opExtrude","SWEPT_FACE",FACE,{"disambiguationData":[OSD([subQ0])]}),makeQuery(id+"F3.opExtrude","SWEPT_FACE",FACE,{"disambiguationData":[OSD([subQ0])]})]}),makeQuery(id+"FehnNMLxcj5brBZ_1.2.F7.opExtrude","SWEPT_FACE",FACE,{"disambiguationData":[OSD([sQuery(id+"F6.wireOp",EDGE,"E10.1.6.0")])]})]});}
            var Q25;
            {var subQ0=sQuery(id+"F0.wireOp",EDGE,"E6.1.0");Q25=makeQuery(id+"FehnNMLxcj5brBZ_1.2.F7.boolean.opBoolean","INTERSECT",EDGE,{"disambiguationData":[OD(1.0)],"derivedFrom":[makeQuery(id+"F3.boolean.opBoolean","MERGE",FACE,{"derivedFrom":[makeQuery(id+"F1.opExtrude","SWEPT_FACE",FACE,{"disambiguationData":[OSD([subQ0])]}),makeQuery(id+"F3.opExtrude","SWEPT_FACE",FACE,{"disambiguationData":[OSD([subQ0])]})]}),makeQuery(id+"FehnNMLxcj5brBZ_1.2.F7.opExtrude","SWEPT_FACE",FACE,{"disambiguationData":[OSD([sQuery(id+"F6.wireOp",EDGE,"E9.5.0")])]})]});}
            var Q26;
            {var subQ0=sQuery(id+"F0.wireOp",EDGE,"E6.1.0");Q26=makeQuery(id+"FehnNMLxcj5brBZ_1.2.F7.boolean.opBoolean","INTERSECT",EDGE,{"disambiguationData":[OD(1.0)],"derivedFrom":[makeQuery(id+"F3.boolean.opBoolean","MERGE",FACE,{"derivedFrom":[makeQuery(id+"F1.opExtrude","SWEPT_FACE",FACE,{"disambiguationData":[OSD([subQ0])]}),makeQuery(id+"F3.opExtrude","SWEPT_FACE",FACE,{"disambiguationData":[OSD([subQ0])]})]}),makeQuery(id+"FehnNMLxcj5brBZ_1.2.F7.opExtrude","SWEPT_FACE",FACE,{"disambiguationData":[OSD([sQuery(id+"F6.wireOp",EDGE,"E9.4.0")])]})]});}
            var Q27;
            {var subQ0=sQuery(id+"F0.wireOp",EDGE,"E6.1.0");Q27=makeQuery(id+"FehnNMLxcj5brBZ_1.2.F7.boolean.opBoolean","INTERSECT",EDGE,{"disambiguationData":[OD(0.0)],"derivedFrom":[makeQuery(id+"F3.boolean.opBoolean","MERGE",FACE,{"derivedFrom":[makeQuery(id+"F1.opExtrude","SWEPT_FACE",FACE,{"disambiguationData":[OSD([subQ0])]}),makeQuery(id+"F3.opExtrude","SWEPT_FACE",FACE,{"disambiguationData":[OSD([subQ0])]})]}),makeQuery(id+"FehnNMLxcj5brBZ_1.2.F7.opExtrude","SWEPT_FACE",FACE,{"disambiguationData":[OSD([sQuery(id+"F6.wireOp",EDGE,"E9.5.0")])]})]});}
            var Q28;
            {var subQ0=sQuery(id+"F0.wireOp",EDGE,"E6.1.0");Q28=makeQuery(id+"FehnNMLxcj5brBZ_1.2.F7.boolean.opBoolean","INTERSECT",EDGE,{"disambiguationData":[OD(0.0)],"derivedFrom":[makeQuery(id+"F3.boolean.opBoolean","MERGE",FACE,{"derivedFrom":[makeQuery(id+"F1.opExtrude","SWEPT_FACE",FACE,{"disambiguationData":[OSD([subQ0])]}),makeQuery(id+"F3.opExtrude","SWEPT_FACE",FACE,{"disambiguationData":[OSD([subQ0])]})]}),makeQuery(id+"FehnNMLxcj5brBZ_1.2.F7.opExtrude","SWEPT_FACE",FACE,{"disambiguationData":[OSD([sQuery(id+"F6.wireOp",EDGE,"E9.4.0")])]})]});}
            var Q29;
            {var subQ0=sQuery(id+"F0.wireOp",EDGE,"E6.1.0");Q29=makeQuery(id+"FehnNMLxcj5brBZ_1.2.F7.boolean.opBoolean","INTERSECT",EDGE,{"disambiguationData":[OD(1.0)],"derivedFrom":[makeQuery(id+"F3.boolean.opBoolean","MERGE",FACE,{"derivedFrom":[makeQuery(id+"F1.opExtrude","SWEPT_FACE",FACE,{"disambiguationData":[OSD([subQ0])]}),makeQuery(id+"F3.opExtrude","SWEPT_FACE",FACE,{"disambiguationData":[OSD([subQ0])]})]}),makeQuery(id+"FehnNMLxcj5brBZ_1.2.F7.opExtrude","SWEPT_FACE",FACE,{"disambiguationData":[OSD([sQuery(id+"F6.wireOp",EDGE,"E9.3.0")])]})]});}
            var Q30;
            {var subQ0=sQuery(id+"F0.wireOp",EDGE,"E6.1.0");Q30=makeQuery(id+"FehnNMLxcj5brBZ_1.2.F7.boolean.opBoolean","INTERSECT",EDGE,{"disambiguationData":[OD(1.0)],"derivedFrom":[makeQuery(id+"F3.boolean.opBoolean","MERGE",FACE,{"derivedFrom":[makeQuery(id+"F1.opExtrude","SWEPT_FACE",FACE,{"disambiguationData":[OSD([subQ0])]}),makeQuery(id+"F3.opExtrude","SWEPT_FACE",FACE,{"disambiguationData":[OSD([subQ0])]})]}),makeQuery(id+"FehnNMLxcj5brBZ_1.2.F7.opExtrude","SWEPT_FACE",FACE,{"disambiguationData":[OSD([sQuery(id+"F6.wireOp",EDGE,"E9.2.0")])]})]});}
            var Q31;
            {var subQ0=sQuery(id+"F0.wireOp",EDGE,"E6.1.0");Q31=makeQuery(id+"FehnNMLxcj5brBZ_1.2.F7.boolean.opBoolean","INTERSECT",EDGE,{"disambiguationData":[OD(0.0)],"derivedFrom":[makeQuery(id+"F3.boolean.opBoolean","MERGE",FACE,{"derivedFrom":[makeQuery(id+"F1.opExtrude","SWEPT_FACE",FACE,{"disambiguationData":[OSD([subQ0])]}),makeQuery(id+"F3.opExtrude","SWEPT_FACE",FACE,{"disambiguationData":[OSD([subQ0])]})]}),makeQuery(id+"FehnNMLxcj5brBZ_1.2.F7.opExtrude","SWEPT_FACE",FACE,{"disambiguationData":[OSD([sQuery(id+"F6.wireOp",EDGE,"E9.3.0")])]})]});}
            var Q32;
            {var subQ0=sQuery(id+"F0.wireOp",EDGE,"E6.1.0");Q32=makeQuery(id+"FehnNMLxcj5brBZ_1.2.F7.boolean.opBoolean","INTERSECT",EDGE,{"disambiguationData":[OD(0.0)],"derivedFrom":[makeQuery(id+"F3.boolean.opBoolean","MERGE",FACE,{"derivedFrom":[makeQuery(id+"F1.opExtrude","SWEPT_FACE",FACE,{"disambiguationData":[OSD([subQ0])]}),makeQuery(id+"F3.opExtrude","SWEPT_FACE",FACE,{"disambiguationData":[OSD([subQ0])]})]}),makeQuery(id+"FehnNMLxcj5brBZ_1.2.F7.opExtrude","SWEPT_FACE",FACE,{"disambiguationData":[OSD([sQuery(id+"F6.wireOp",EDGE,"E9.2.0")])]})]});}
            var Q33;
            {var subQ0=sQuery(id+"F0.wireOp",EDGE,"E6.1.0");Q33=makeQuery(id+"FehnNMLxcj5brBZ_1.2.F7.boolean.opBoolean","INTERSECT",EDGE,{"disambiguationData":[OD(1.0)],"derivedFrom":[makeQuery(id+"F3.boolean.opBoolean","MERGE",FACE,{"derivedFrom":[makeQuery(id+"F1.opExtrude","SWEPT_FACE",FACE,{"disambiguationData":[OSD([subQ0])]}),makeQuery(id+"F3.opExtrude","SWEPT_FACE",FACE,{"disambiguationData":[OSD([subQ0])]})]}),makeQuery(id+"FehnNMLxcj5brBZ_1.2.F7.opExtrude","SWEPT_FACE",FACE,{"disambiguationData":[OSD([sQuery(id+"F6.wireOp",EDGE,"E9.1.0")])]})]});}
            var Q34;
            {var subQ0=sQuery(id+"F0.wireOp",EDGE,"E6.1.0");Q34=makeQuery(id+"FehnNMLxcj5brBZ_1.2.F7.boolean.opBoolean","INTERSECT",EDGE,{"disambiguationData":[OD(0.0)],"derivedFrom":[makeQuery(id+"F3.boolean.opBoolean","MERGE",FACE,{"derivedFrom":[makeQuery(id+"F1.opExtrude","SWEPT_FACE",FACE,{"disambiguationData":[OSD([subQ0])]}),makeQuery(id+"F3.opExtrude","SWEPT_FACE",FACE,{"disambiguationData":[OSD([subQ0])]})]}),makeQuery(id+"FehnNMLxcj5brBZ_1.2.F7.opExtrude","SWEPT_FACE",FACE,{"disambiguationData":[OSD([sQuery(id+"F6.wireOp",EDGE,"E9.1.0")])]})]});}
            var Q35;
            {var subQ0=sQuery(id+"F0.wireOp",EDGE,"E6.1.0");Q35=makeQuery(id+"FehnNMLxcj5brBZ_1.2.F7.boolean.opBoolean","INTERSECT",EDGE,{"derivedFrom":[makeQuery(id+"F3.boolean.opBoolean","MERGE",FACE,{"derivedFrom":[makeQuery(id+"F1.opExtrude","SWEPT_FACE",FACE,{"disambiguationData":[OSD([subQ0])]}),makeQuery(id+"F3.opExtrude","SWEPT_FACE",FACE,{"disambiguationData":[OSD([subQ0])]})]}),makeQuery(id+"FehnNMLxcj5brBZ_1.2.F7.opExtrude","SWEPT_FACE",FACE,{"disambiguationData":[OSD([sQuery(id+"F6.wireOp",EDGE,"E8")])]})]});}
            var Q36;
            {var subQ0=sQuery(id+"F0.wireOp",EDGE,"E6.2.0");Q36=makeQuery(id+"FehnNMLxcj5brBZ_1.1.F7.boolean.opBoolean","INTERSECT",EDGE,{"derivedFrom":[makeQuery(id+"F3.boolean.opBoolean","MERGE",FACE,{"derivedFrom":[makeQuery(id+"F1.opExtrude","SWEPT_FACE",FACE,{"disambiguationData":[OSD([subQ0])]}),makeQuery(id+"F3.opExtrude","SWEPT_FACE",FACE,{"disambiguationData":[OSD([subQ0])]})]}),makeQuery(id+"FehnNMLxcj5brBZ_1.1.F7.opExtrude","SWEPT_FACE",FACE,{"disambiguationData":[OSD([sQuery(id+"F6.wireOp",EDGE,"E10.1.9.0")])]})]});}
            var Q37;
            {var subQ0=sQuery(id+"F0.wireOp",EDGE,"E6.2.0");Q37=makeQuery(id+"FehnNMLxcj5brBZ_1.1.F7.boolean.opBoolean","INTERSECT",EDGE,{"disambiguationData":[OD(1.0)],"derivedFrom":[makeQuery(id+"F3.boolean.opBoolean","MERGE",FACE,{"derivedFrom":[makeQuery(id+"F1.opExtrude","SWEPT_FACE",FACE,{"disambiguationData":[OSD([subQ0])]}),makeQuery(id+"F3.opExtrude","SWEPT_FACE",FACE,{"disambiguationData":[OSD([subQ0])]})]}),makeQuery(id+"FehnNMLxcj5brBZ_1.1.F7.opExtrude","SWEPT_FACE",FACE,{"disambiguationData":[OSD([sQuery(id+"F6.wireOp",EDGE,"E10.1.8.0")])]})]});}
            var Q38;
            {var subQ0=sQuery(id+"F0.wireOp",EDGE,"E6.2.0");Q38=makeQuery(id+"FehnNMLxcj5brBZ_1.1.F7.boolean.opBoolean","INTERSECT",EDGE,{"disambiguationData":[OD(0.0)],"derivedFrom":[makeQuery(id+"F3.boolean.opBoolean","MERGE",FACE,{"derivedFrom":[makeQuery(id+"F1.opExtrude","SWEPT_FACE",FACE,{"disambiguationData":[OSD([subQ0])]}),makeQuery(id+"F3.opExtrude","SWEPT_FACE",FACE,{"disambiguationData":[OSD([subQ0])]})]}),makeQuery(id+"FehnNMLxcj5brBZ_1.1.F7.opExtrude","SWEPT_FACE",FACE,{"disambiguationData":[OSD([sQuery(id+"F6.wireOp",EDGE,"E10.1.8.0")])]})]});}
            var Q39;
            {var subQ0=sQuery(id+"F0.wireOp",EDGE,"E6.2.0");Q39=makeQuery(id+"FehnNMLxcj5brBZ_1.1.F7.boolean.opBoolean","INTERSECT",EDGE,{"disambiguationData":[OD(0.0)],"derivedFrom":[makeQuery(id+"F3.boolean.opBoolean","MERGE",FACE,{"derivedFrom":[makeQuery(id+"F1.opExtrude","SWEPT_FACE",FACE,{"disambiguationData":[OSD([subQ0])]}),makeQuery(id+"F3.opExtrude","SWEPT_FACE",FACE,{"disambiguationData":[OSD([subQ0])]})]}),makeQuery(id+"FehnNMLxcj5brBZ_1.1.F7.opExtrude","SWEPT_FACE",FACE,{"disambiguationData":[OSD([sQuery(id+"F6.wireOp",EDGE,"E10.1.7.0")])]})]});}
            var Q40;
            {var subQ0=sQuery(id+"F0.wireOp",EDGE,"E6.2.0");Q40=makeQuery(id+"FehnNMLxcj5brBZ_1.1.F7.boolean.opBoolean","INTERSECT",EDGE,{"disambiguationData":[OD(1.0)],"derivedFrom":[makeQuery(id+"F3.boolean.opBoolean","MERGE",FACE,{"derivedFrom":[makeQuery(id+"F1.opExtrude","SWEPT_FACE",FACE,{"disambiguationData":[OSD([subQ0])]}),makeQuery(id+"F3.opExtrude","SWEPT_FACE",FACE,{"disambiguationData":[OSD([subQ0])]})]}),makeQuery(id+"FehnNMLxcj5brBZ_1.1.F7.opExtrude","SWEPT_FACE",FACE,{"disambiguationData":[OSD([sQuery(id+"F6.wireOp",EDGE,"E10.1.7.0")])]})]});}
            var Q41;
            {var subQ0=sQuery(id+"F0.wireOp",EDGE,"E6.2.0");Q41=makeQuery(id+"FehnNMLxcj5brBZ_1.1.F7.boolean.opBoolean","INTERSECT",EDGE,{"disambiguationData":[OD(1.0)],"derivedFrom":[makeQuery(id+"F3.boolean.opBoolean","MERGE",FACE,{"derivedFrom":[makeQuery(id+"F1.opExtrude","SWEPT_FACE",FACE,{"disambiguationData":[OSD([subQ0])]}),makeQuery(id+"F3.opExtrude","SWEPT_FACE",FACE,{"disambiguationData":[OSD([subQ0])]})]}),makeQuery(id+"FehnNMLxcj5brBZ_1.1.F7.opExtrude","SWEPT_FACE",FACE,{"disambiguationData":[OSD([sQuery(id+"F6.wireOp",EDGE,"E10.1.6.0")])]})]});}
            var Q42;
            {var subQ0=sQuery(id+"F0.wireOp",EDGE,"E6.2.0");Q42=makeQuery(id+"FehnNMLxcj5brBZ_1.1.F7.boolean.opBoolean","INTERSECT",EDGE,{"disambiguationData":[OD(0.0)],"derivedFrom":[makeQuery(id+"F3.boolean.opBoolean","MERGE",FACE,{"derivedFrom":[makeQuery(id+"F1.opExtrude","SWEPT_FACE",FACE,{"disambiguationData":[OSD([subQ0])]}),makeQuery(id+"F3.opExtrude","SWEPT_FACE",FACE,{"disambiguationData":[OSD([subQ0])]})]}),makeQuery(id+"FehnNMLxcj5brBZ_1.1.F7.opExtrude","SWEPT_FACE",FACE,{"disambiguationData":[OSD([sQuery(id+"F6.wireOp",EDGE,"E10.1.6.0")])]})]});}
            var Q43;
            {var subQ0=sQuery(id+"F0.wireOp",EDGE,"E6.2.0");Q43=makeQuery(id+"FehnNMLxcj5brBZ_1.1.F7.boolean.opBoolean","INTERSECT",EDGE,{"disambiguationData":[OD(1.0)],"derivedFrom":[makeQuery(id+"F3.boolean.opBoolean","MERGE",FACE,{"derivedFrom":[makeQuery(id+"F1.opExtrude","SWEPT_FACE",FACE,{"disambiguationData":[OSD([subQ0])]}),makeQuery(id+"F3.opExtrude","SWEPT_FACE",FACE,{"disambiguationData":[OSD([subQ0])]})]}),makeQuery(id+"FehnNMLxcj5brBZ_1.1.F7.opExtrude","SWEPT_FACE",FACE,{"disambiguationData":[OSD([sQuery(id+"F6.wireOp",EDGE,"E9.5.0")])]})]});}
            var Q44;
            {var subQ0=sQuery(id+"F0.wireOp",EDGE,"E6.2.0");Q44=makeQuery(id+"FehnNMLxcj5brBZ_1.1.F7.boolean.opBoolean","INTERSECT",EDGE,{"disambiguationData":[OD(0.0)],"derivedFrom":[makeQuery(id+"F3.boolean.opBoolean","MERGE",FACE,{"derivedFrom":[makeQuery(id+"F1.opExtrude","SWEPT_FACE",FACE,{"disambiguationData":[OSD([subQ0])]}),makeQuery(id+"F3.opExtrude","SWEPT_FACE",FACE,{"disambiguationData":[OSD([subQ0])]})]}),makeQuery(id+"FehnNMLxcj5brBZ_1.1.F7.opExtrude","SWEPT_FACE",FACE,{"disambiguationData":[OSD([sQuery(id+"F6.wireOp",EDGE,"E9.5.0")])]})]});}
            var Q45;
            {var subQ0=sQuery(id+"F0.wireOp",EDGE,"E6.2.0");Q45=makeQuery(id+"FehnNMLxcj5brBZ_1.1.F7.boolean.opBoolean","INTERSECT",EDGE,{"disambiguationData":[OD(1.0)],"derivedFrom":[makeQuery(id+"F3.boolean.opBoolean","MERGE",FACE,{"derivedFrom":[makeQuery(id+"F1.opExtrude","SWEPT_FACE",FACE,{"disambiguationData":[OSD([subQ0])]}),makeQuery(id+"F3.opExtrude","SWEPT_FACE",FACE,{"disambiguationData":[OSD([subQ0])]})]}),makeQuery(id+"FehnNMLxcj5brBZ_1.1.F7.opExtrude","SWEPT_FACE",FACE,{"disambiguationData":[OSD([sQuery(id+"F6.wireOp",EDGE,"E9.4.0")])]})]});}
            var Q46;
            {var subQ0=sQuery(id+"F0.wireOp",EDGE,"E6.2.0");Q46=makeQuery(id+"FehnNMLxcj5brBZ_1.1.F7.boolean.opBoolean","INTERSECT",EDGE,{"disambiguationData":[OD(0.0)],"derivedFrom":[makeQuery(id+"F3.boolean.opBoolean","MERGE",FACE,{"derivedFrom":[makeQuery(id+"F1.opExtrude","SWEPT_FACE",FACE,{"disambiguationData":[OSD([subQ0])]}),makeQuery(id+"F3.opExtrude","SWEPT_FACE",FACE,{"disambiguationData":[OSD([subQ0])]})]}),makeQuery(id+"FehnNMLxcj5brBZ_1.1.F7.opExtrude","SWEPT_FACE",FACE,{"disambiguationData":[OSD([sQuery(id+"F6.wireOp",EDGE,"E9.4.0")])]})]});}
            var Q47;
            {var subQ0=sQuery(id+"F0.wireOp",EDGE,"E6.2.0");Q47=makeQuery(id+"FehnNMLxcj5brBZ_1.1.F7.boolean.opBoolean","INTERSECT",EDGE,{"disambiguationData":[OD(1.0)],"derivedFrom":[makeQuery(id+"F3.boolean.opBoolean","MERGE",FACE,{"derivedFrom":[makeQuery(id+"F1.opExtrude","SWEPT_FACE",FACE,{"disambiguationData":[OSD([subQ0])]}),makeQuery(id+"F3.opExtrude","SWEPT_FACE",FACE,{"disambiguationData":[OSD([subQ0])]})]}),makeQuery(id+"FehnNMLxcj5brBZ_1.1.F7.opExtrude","SWEPT_FACE",FACE,{"disambiguationData":[OSD([sQuery(id+"F6.wireOp",EDGE,"E9.3.0")])]})]});}
            var Q48;
            {var subQ0=sQuery(id+"F0.wireOp",EDGE,"E6.2.0");Q48=makeQuery(id+"FehnNMLxcj5brBZ_1.1.F7.boolean.opBoolean","INTERSECT",EDGE,{"disambiguationData":[OD(0.0)],"derivedFrom":[makeQuery(id+"F3.boolean.opBoolean","MERGE",FACE,{"derivedFrom":[makeQuery(id+"F1.opExtrude","SWEPT_FACE",FACE,{"disambiguationData":[OSD([subQ0])]}),makeQuery(id+"F3.opExtrude","SWEPT_FACE",FACE,{"disambiguationData":[OSD([subQ0])]})]}),makeQuery(id+"FehnNMLxcj5brBZ_1.1.F7.opExtrude","SWEPT_FACE",FACE,{"disambiguationData":[OSD([sQuery(id+"F6.wireOp",EDGE,"E9.3.0")])]})]});}
            var Q49;
            {var subQ0=sQuery(id+"F0.wireOp",EDGE,"E6.2.0");Q49=makeQuery(id+"FehnNMLxcj5brBZ_1.1.F7.boolean.opBoolean","INTERSECT",EDGE,{"disambiguationData":[OD(1.0)],"derivedFrom":[makeQuery(id+"F3.boolean.opBoolean","MERGE",FACE,{"derivedFrom":[makeQuery(id+"F1.opExtrude","SWEPT_FACE",FACE,{"disambiguationData":[OSD([subQ0])]}),makeQuery(id+"F3.opExtrude","SWEPT_FACE",FACE,{"disambiguationData":[OSD([subQ0])]})]}),makeQuery(id+"FehnNMLxcj5brBZ_1.1.F7.opExtrude","SWEPT_FACE",FACE,{"disambiguationData":[OSD([sQuery(id+"F6.wireOp",EDGE,"E9.2.0")])]})]});}
            var Q50;
            {var subQ0=sQuery(id+"F0.wireOp",EDGE,"E6.2.0");Q50=makeQuery(id+"FehnNMLxcj5brBZ_1.1.F7.boolean.opBoolean","INTERSECT",EDGE,{"disambiguationData":[OD(0.0)],"derivedFrom":[makeQuery(id+"F3.boolean.opBoolean","MERGE",FACE,{"derivedFrom":[makeQuery(id+"F1.opExtrude","SWEPT_FACE",FACE,{"disambiguationData":[OSD([subQ0])]}),makeQuery(id+"F3.opExtrude","SWEPT_FACE",FACE,{"disambiguationData":[OSD([subQ0])]})]}),makeQuery(id+"FehnNMLxcj5brBZ_1.1.F7.opExtrude","SWEPT_FACE",FACE,{"disambiguationData":[OSD([sQuery(id+"F6.wireOp",EDGE,"E9.2.0")])]})]});}
            var Q51;
            {var subQ0=sQuery(id+"F0.wireOp",EDGE,"E6.2.0");Q51=makeQuery(id+"FehnNMLxcj5brBZ_1.1.F7.boolean.opBoolean","INTERSECT",EDGE,{"disambiguationData":[OD(1.0)],"derivedFrom":[makeQuery(id+"F3.boolean.opBoolean","MERGE",FACE,{"derivedFrom":[makeQuery(id+"F1.opExtrude","SWEPT_FACE",FACE,{"disambiguationData":[OSD([subQ0])]}),makeQuery(id+"F3.opExtrude","SWEPT_FACE",FACE,{"disambiguationData":[OSD([subQ0])]})]}),makeQuery(id+"FehnNMLxcj5brBZ_1.1.F7.opExtrude","SWEPT_FACE",FACE,{"disambiguationData":[OSD([sQuery(id+"F6.wireOp",EDGE,"E9.1.0")])]})]});}
            var Q52;
            {var subQ0=sQuery(id+"F0.wireOp",EDGE,"E6.2.0");Q52=makeQuery(id+"FehnNMLxcj5brBZ_1.1.F7.boolean.opBoolean","INTERSECT",EDGE,{"derivedFrom":[makeQuery(id+"F3.boolean.opBoolean","MERGE",FACE,{"derivedFrom":[makeQuery(id+"F1.opExtrude","SWEPT_FACE",FACE,{"disambiguationData":[OSD([subQ0])]}),makeQuery(id+"F3.opExtrude","SWEPT_FACE",FACE,{"disambiguationData":[OSD([subQ0])]})]}),makeQuery(id+"FehnNMLxcj5brBZ_1.1.F7.opExtrude","SWEPT_FACE",FACE,{"disambiguationData":[OSD([sQuery(id+"F6.wireOp",EDGE,"E8")])]})]});}
            var Q53;
            {var subQ0=sQuery(id+"F0.wireOp",EDGE,"E6.2.0");Q53=makeQuery(id+"FehnNMLxcj5brBZ_1.1.F7.boolean.opBoolean","INTERSECT",EDGE,{"disambiguationData":[OD(0.0)],"derivedFrom":[makeQuery(id+"F3.boolean.opBoolean","MERGE",FACE,{"derivedFrom":[makeQuery(id+"F1.opExtrude","SWEPT_FACE",FACE,{"disambiguationData":[OSD([subQ0])]}),makeQuery(id+"F3.opExtrude","SWEPT_FACE",FACE,{"disambiguationData":[OSD([subQ0])]})]}),makeQuery(id+"FehnNMLxcj5brBZ_1.1.F7.opExtrude","SWEPT_FACE",FACE,{"disambiguationData":[OSD([sQuery(id+"F6.wireOp",EDGE,"E9.1.0")])]})]});}
            fillet(context, id + "F8", {"entities" : qUnion([Q0, Q1, Q2, Q3, Q4, Q5, Q6, Q7, Q8, Q9, Q10, Q11, Q12, Q13, Q14, Q15, Q16, Q17, Q18, Q19, Q20, Q21, Q22, Q23, Q24, Q25, Q26, Q27, Q28, Q29, Q30, Q31, Q32, Q33, Q34, Q35, Q36, Q37, Q38, Q39, Q40, Q41, Q42, Q43, Q44, Q45, Q46, Q47, Q48, Q49, Q50, Q51, Q52, Q53]), "radius" : 1 * mm, "tangentPropagation" : true, "allowEdgeOverflow" : false});
        }
        {
            var Q0;
            {var subQ0=sQuery(id+"F0.wireOp",EDGE,"E4");Q0=makeQuery(id+"F7.boolean.opBoolean","INTERSECT",EDGE,{"derivedFrom":[makeQuery(id+"F3.boolean.opBoolean","MERGE",FACE,{"derivedFrom":[makeQuery(id+"F1.opExtrude","SWEPT_FACE",FACE,{"disambiguationData":[OSD([subQ0])]}),makeQuery(id+"F3.opExtrude","SWEPT_FACE",FACE,{"disambiguationData":[OSD([subQ0])]})]}),makeQuery(id+"F7.opExtrude","SWEPT_FACE",FACE,{"disambiguationData":[OSD([sQuery(id+"F6.wireOp",EDGE,"E8")])]})]});}
            var Q1;
            {var subQ0=sQuery(id+"F0.wireOp",EDGE,"E5");Q1=makeQuery(id+"F7.boolean.opBoolean","INTERSECT",EDGE,{"derivedFrom":[makeQuery(id+"F3.boolean.opBoolean","MERGE",FACE,{"derivedFrom":[makeQuery(id+"F1.opExtrude","SWEPT_FACE",FACE,{"disambiguationData":[OSD([subQ0])]}),makeQuery(id+"F3.opExtrude","SWEPT_FACE",FACE,{"disambiguationData":[OSD([subQ0])]})]}),makeQuery(id+"F7.opExtrude","SWEPT_FACE",FACE,{"disambiguationData":[OSD([sQuery(id+"F6.wireOp",EDGE,"E10.1.9.0")])]})]});}
            var Q2;
            {var subQ0=sQuery(id+"F0.wireOp",EDGE,"E6.2.7");Q2=makeQuery(id+"FehnNMLxcj5brBZ_1.1.F7.boolean.opBoolean","INTERSECT",EDGE,{"derivedFrom":[makeQuery(id+"F3.boolean.opBoolean","MERGE",FACE,{"derivedFrom":[makeQuery(id+"F1.opExtrude","SWEPT_FACE",FACE,{"disambiguationData":[OSD([subQ0])]}),makeQuery(id+"F3.opExtrude","SWEPT_FACE",FACE,{"disambiguationData":[OSD([subQ0])]})]}),makeQuery(id+"FehnNMLxcj5brBZ_1.1.F7.opExtrude","SWEPT_FACE",FACE,{"disambiguationData":[OSD([sQuery(id+"F6.wireOp",EDGE,"E8")])]})]});}
            var Q3;
            {var subQ0=sQuery(id+"F0.wireOp",EDGE,"E6.2.8");Q3=makeQuery(id+"FehnNMLxcj5brBZ_1.1.F7.boolean.opBoolean","INTERSECT",EDGE,{"derivedFrom":[makeQuery(id+"F3.boolean.opBoolean","MERGE",FACE,{"derivedFrom":[makeQuery(id+"F1.opExtrude","SWEPT_FACE",FACE,{"disambiguationData":[OSD([subQ0])]}),makeQuery(id+"F3.opExtrude","SWEPT_FACE",FACE,{"disambiguationData":[OSD([subQ0])]})]}),makeQuery(id+"FehnNMLxcj5brBZ_1.1.F7.opExtrude","SWEPT_FACE",FACE,{"disambiguationData":[OSD([sQuery(id+"F6.wireOp",EDGE,"E10.1.9.0")])]})]});}
            var Q4;
            {var subQ0=sQuery(id+"F0.wireOp",EDGE,"E6.1.7");Q4=makeQuery(id+"FehnNMLxcj5brBZ_1.2.F7.boolean.opBoolean","INTERSECT",EDGE,{"derivedFrom":[makeQuery(id+"F3.boolean.opBoolean","MERGE",FACE,{"derivedFrom":[makeQuery(id+"F1.opExtrude","SWEPT_FACE",FACE,{"disambiguationData":[OSD([subQ0])]}),makeQuery(id+"F3.opExtrude","SWEPT_FACE",FACE,{"disambiguationData":[OSD([subQ0])]})]}),makeQuery(id+"FehnNMLxcj5brBZ_1.2.F7.opExtrude","SWEPT_FACE",FACE,{"disambiguationData":[OSD([sQuery(id+"F6.wireOp",EDGE,"E8")])]})]});}
            var Q5;
            {var subQ0=sQuery(id+"F0.wireOp",EDGE,"E6.1.8");Q5=makeQuery(id+"FehnNMLxcj5brBZ_1.2.F7.boolean.opBoolean","INTERSECT",EDGE,{"derivedFrom":[makeQuery(id+"F3.boolean.opBoolean","MERGE",FACE,{"derivedFrom":[makeQuery(id+"F1.opExtrude","SWEPT_FACE",FACE,{"disambiguationData":[OSD([subQ0])]}),makeQuery(id+"F3.opExtrude","SWEPT_FACE",FACE,{"disambiguationData":[OSD([subQ0])]})]}),makeQuery(id+"FehnNMLxcj5brBZ_1.2.F7.opExtrude","SWEPT_FACE",FACE,{"disambiguationData":[OSD([sQuery(id+"F6.wireOp",EDGE,"E10.1.9.0")])]})]});}
            fillet(context, id + "F9", {"entities" : qUnion([Q0, Q1, Q2, Q3, Q4, Q5]), "radius" : 20 * mm, "tangentPropagation" : true, "allowEdgeOverflow" : false});
        }
        {
            var Q0;
            {var subQ0=sQuery(id+"F6.wireOp",EDGE,"E10.1.9.0");var subQ1=sQuery(id+"F6.wireOp",EDGE,"E10.1.8.0");var subQ2=sQuery(id+"F6.wireOp",EDGE,"E10.1.7.0");var subQ3=sQuery(id+"F6.wireOp",EDGE,"E10.1.6.0");var subQ4=sQuery(id+"F6.wireOp",EDGE,"E9.5.0");var subQ5=sQuery(id+"F6.wireOp",EDGE,"E9.4.0");var subQ6=sQuery(id+"F6.wireOp",EDGE,"E9.3.0");var subQ7=sQuery(id+"F6.wireOp",EDGE,"E9.2.0");var subQ8=sQuery(id+"F6.wireOp",EDGE,"E9.1.0");var subQ9=sQuery(id+"F6.wireOp",EDGE,"E8");Q0=makeQuery(id+"FehnNMLxcj5brBZ_1.2.F7.boolean.opBoolean","MERGE",FACE,{"derivedFrom":[makeQuery(id+"FehnNMLxcj5brBZ_1.1.F7.boolean.opBoolean","MERGE",FACE,{"derivedFrom":[makeQuery(id+"F7.boolean.opBoolean","MERGE",FACE,{"derivedFrom":[makeQuery(id+"F3.opExtrude","CAP_FACE",FACE,{"disambiguationData":[OSD([sQuery(id+"F0.wireOp",EDGE,"E2"),sQuery(id+"F0.wireOp",EDGE,"E4"),sQuery(id+"F0.wireOp",EDGE,"E5"),sQuery(id+"F0.wireOp",EDGE,"E6.1.0"),sQuery(id+"F0.wireOp",EDGE,"E6.1.7"),sQuery(id+"F0.wireOp",EDGE,"E6.1.8"),sQuery(id+"F0.wireOp",EDGE,"E6.2.0"),sQuery(id+"F0.wireOp",EDGE,"E6.2.7"),sQuery(id+"F0.wireOp",EDGE,"E6.2.8"),sQuery(id+"F2.wireOp",EDGE,"E7")])],"isStart":false}),makeQuery(id+"F7.opExtrude","CAP_FACE",FACE,{"disambiguationData":[OSD([subQ9])],"isStart":true}),makeQuery(id+"F7.opExtrude","CAP_FACE",FACE,{"disambiguationData":[OSD([subQ8])],"isStart":true}),makeQuery(id+"F7.opExtrude","CAP_FACE",FACE,{"disambiguationData":[OSD([subQ7])],"isStart":true}),makeQuery(id+"F7.opExtrude","CAP_FACE",FACE,{"disambiguationData":[OSD([subQ6])],"isStart":true}),makeQuery(id+"F7.opExtrude","CAP_FACE",FACE,{"disambiguationData":[OSD([subQ5])],"isStart":true}),makeQuery(id+"F7.opExtrude","CAP_FACE",FACE,{"disambiguationData":[OSD([subQ4])],"isStart":true}),makeQuery(id+"F7.opExtrude","CAP_FACE",FACE,{"disambiguationData":[OSD([subQ3])],"isStart":true}),makeQuery(id+"F7.opExtrude","CAP_FACE",FACE,{"disambiguationData":[OSD([subQ2])],"isStart":true}),makeQuery(id+"F7.opExtrude","CAP_FACE",FACE,{"disambiguationData":[OSD([subQ1])],"isStart":true}),makeQuery(id+"F7.opExtrude","CAP_FACE",FACE,{"disambiguationData":[OSD([subQ0])],"isStart":true})]}),makeQuery(id+"FehnNMLxcj5brBZ_1.1.F7.opExtrude","CAP_FACE",FACE,{"disambiguationData":[OSD([subQ9])],"isStart":true}),makeQuery(id+"FehnNMLxcj5brBZ_1.1.F7.opExtrude","CAP_FACE",FACE,{"disambiguationData":[OSD([subQ8])],"isStart":true}),makeQuery(id+"FehnNMLxcj5brBZ_1.1.F7.opExtrude","CAP_FACE",FACE,{"disambiguationData":[OSD([subQ7])],"isStart":true}),makeQuery(id+"FehnNMLxcj5brBZ_1.1.F7.opExtrude","CAP_FACE",FACE,{"disambiguationData":[OSD([subQ6])],"isStart":true}),makeQuery(id+"FehnNMLxcj5brBZ_1.1.F7.opExtrude","CAP_FACE",FACE,{"disambiguationData":[OSD([subQ5])],"isStart":true}),makeQuery(id+"FehnNMLxcj5brBZ_1.1.F7.opExtrude","CAP_FACE",FACE,{"disambiguationData":[OSD([subQ4])],"isStart":true}),makeQuery(id+"FehnNMLxcj5brBZ_1.1.F7.opExtrude","CAP_FACE",FACE,{"disambiguationData":[OSD([subQ3])],"isStart":true}),makeQuery(id+"FehnNMLxcj5brBZ_1.1.F7.opExtrude","CAP_FACE",FACE,{"disambiguationData":[OSD([subQ2])],"isStart":true}),makeQuery(id+"FehnNMLxcj5brBZ_1.1.F7.opExtrude","CAP_FACE",FACE,{"disambiguationData":[OSD([subQ1])],"isStart":true}),makeQuery(id+"FehnNMLxcj5brBZ_1.1.F7.opExtrude","CAP_FACE",FACE,{"disambiguationData":[OSD([subQ0])],"isStart":true})]}),makeQuery(id+"FehnNMLxcj5brBZ_1.2.F7.opExtrude","CAP_FACE",FACE,{"disambiguationData":[OSD([subQ9])],"isStart":true}),makeQuery(id+"FehnNMLxcj5brBZ_1.2.F7.opExtrude","CAP_FACE",FACE,{"disambiguationData":[OSD([subQ8])],"isStart":true}),makeQuery(id+"FehnNMLxcj5brBZ_1.2.F7.opExtrude","CAP_FACE",FACE,{"disambiguationData":[OSD([subQ7])],"isStart":true}),makeQuery(id+"FehnNMLxcj5brBZ_1.2.F7.opExtrude","CAP_FACE",FACE,{"disambiguationData":[OSD([subQ6])],"isStart":true}),makeQuery(id+"FehnNMLxcj5brBZ_1.2.F7.opExtrude","CAP_FACE",FACE,{"disambiguationData":[OSD([subQ5])],"isStart":true}),makeQuery(id+"FehnNMLxcj5brBZ_1.2.F7.opExtrude","CAP_FACE",FACE,{"disambiguationData":[OSD([subQ4])],"isStart":true}),makeQuery(id+"FehnNMLxcj5brBZ_1.2.F7.opExtrude","CAP_FACE",FACE,{"disambiguationData":[OSD([subQ3])],"isStart":true}),makeQuery(id+"FehnNMLxcj5brBZ_1.2.F7.opExtrude","CAP_FACE",FACE,{"disambiguationData":[OSD([subQ2])],"isStart":true}),makeQuery(id+"FehnNMLxcj5brBZ_1.2.F7.opExtrude","CAP_FACE",FACE,{"disambiguationData":[OSD([subQ1])],"isStart":true}),makeQuery(id+"FehnNMLxcj5brBZ_1.2.F7.opExtrude","CAP_FACE",FACE,{"disambiguationData":[OSD([subQ0])],"isStart":true})]});}
            chamfer(context, id + "F10", {"entities" : qUnion([Q0]), "width" : 1.2 * mm, "tangentPropagation" : true});
        }
        {
            var Q0;
            Q0=qCreatedBy(makeId("Front.planeOp"),FACE);
            var sketch = newSketch(context, id + "F11", { "sketchPlane" : qUnion([Q0])});
            skLineSegment(sketch, "E11", {"start": v(-7.1, -2) * mm, "end": v(-5.9, -0.8) * mm});
            skLineSegment(sketch, "E12", {"start": v(5.9, -0.8) * mm, "end": v(7.1, -2) * mm});
            skLineSegment(sketch, "E13", {"start": v(5.9, 0.9) * mm, "end": v(5.9, -0.8) * mm});
            skLineSegment(sketch, "E14", {"start": v(-5.9, -0.8) * mm, "end": v(-5.9, 0.9) * mm});
            skLineSegment(sketch, "E15", {"start": v(-6.5, 0.9) * mm, "end": v(-6.5, 4.2) * mm});
            skLineSegment(sketch, "E16", {"start": v(6.5, 4.2) * mm, "end": v(6.5, 0.9) * mm});
            skLineSegment(sketch, "E17.0", {"start": v(-6.77, -2.8) * mm, "end": v(-5.1, -1.13) * mm});
            skLineSegment(sketch, "E18.0", {"start": v(-5.1, -1.13) * mm, "end": v(-5.1, 0.9) * mm});
            skLineSegment(sketch, "E19", {"start": v(-2.4, -5.1) * mm, "end": v(-2.4, 0.9) * mm});
            skLineSegment(sketch, "E20", {"start": v(-6.77, -2.8) * mm, "end": v(-15, -2.8) * mm});
            skLineSegment(sketch, "E21", {"start": v(-15, -2.8) * mm, "end": v(-15, -10.6) * mm});
            skLineSegment(sketch, "E22", {"start": v(-15, -10.6) * mm, "end": v(-3.9, -10.6) * mm});
            skLineSegment(sketch, "E23", {"start": v(-3.9, -10.6) * mm, "end": v(-3.9, -5.1) * mm});
            skLineSegment(sketch, "E24", {"start": v(-3.9, -5.1) * mm, "end": v(-2.4, -5.1) * mm});
            skLineSegment(sketch, "E25", {"start": v(-5.1, 0.9) * mm, "end": v(-2.4, 0.9) * mm});
            skFitSpline(sketch, "E26", {"points": [v(-12.5, -10.6) * mm, v(-3.9, -9.1) * mm], "startDerivative": vector(5, 0) * mm, "endDerivative": vector(20.65, 0.15) * mm});
            skFitSpline(sketch, "E27.0", {"points": [v(-12.5, -11.4) * mm, v(-12.23, -11.4) * mm, v(-11.74, -11.34) * mm, v(-11.12, -11.12) * mm, v(-10.57, -10.88) * mm, v(-9.94, -10.63) * mm, v(-9.08, -10.37) * mm, v(-7.47, -10.06) * mm, v(-5.59, -9.91) * mm, v(-3.9, -9.9) * mm]});
            skSolve(sketch);
        }
        {
            var Q0;
            Q0=makeQuery(id+"F11.imprint","IMPRINT",FACE,{"disambiguationData":[TD([[makeQuery(id+"F11.imprint","IMPRINT",EDGE,{"derivedFrom":sQuery(id+"F11.wireOp",EDGE,"E17.0")}),-1.0]])]});
            var Q1;
            {var subQ0=sQuery(id+"F11.wireOp",EDGE,"E23");var subQ1=sQuery(id+"F11.wireOp",EDGE,"E22");var subQ2=makeQuery(id+"F11.imprint","INTERSECT",VERTEX,{"derivedFrom":[subQ1,subQ0]});Q1=makeQuery(id+"F11.imprint","IMPRINT",FACE,{"disambiguationData":[TD([[makeQuery(id+"F11.imprint","IMPRINT",EDGE,{"disambiguationData":[TD([[subQ2,1.0]])],"derivedFrom":subQ1}),1.0]])]});}
            var Q2;
            {var subQ0=sQuery(id+"F2.wireOp",EDGE,"E7");Q2=makeQuery(id+"F4.boolean.opBoolean","MERGE",FACE,{"derivedFrom":[makeQuery(id+"F3.opExtrude","SWEPT_FACE",FACE,{"disambiguationData":[OSD([subQ0])]}),makeQuery(id+"F4.opExtrude","SWEPT_FACE",FACE,{"disambiguationData":[OSD([subQ0])]})]});}
            revolve(context, id + "F12", {"surfaceOperationType" : NewSurfaceOperationType.NEW, "entities" : qUnion([Q0, Q1]), "axis" : qUnion([Q2]), "revolveType" : RevolveType.FULL});
        }
        {
            var Q0;
            Q0=makeQuery(id+"F12.opRevolve","SWEPT_EDGE",EDGE,{"disambiguationData":[OSD([sQuery(id+"F11.wireOp",EDGE,"E21"),sQuery(id+"F11.wireOp",EDGE,"E22")])]});
            var Q1;
            Q1=makeQuery(id+"F12.opRevolve","SWEPT_EDGE",EDGE,{"disambiguationData":[OSD([sQuery(id+"F11.wireOp",EDGE,"E20"),sQuery(id+"F11.wireOp",EDGE,"E21")])]});
            chamfer(context, id + "F13", {"entities" : qUnion([Q0, Q1]), "width" : 1 * mm, "tangentPropagation" : true});
        }
        {
            var Q0;
            {var subQ0=sQuery(id+"F11.wireOp",EDGE,"E21");Q0=makeQuery(id+"F13.opChamfer","BLEND_EDGE",EDGE,{"blendedFrom":[makeQuery(id+"F12.opRevolve","SWEPT_EDGE",EDGE,{"disambiguationData":[OSD([subQ0,sQuery(id+"F11.wireOp",EDGE,"E22")])]}),makeQuery(id+"F12.opRevolve","SWEPT_FACE",FACE,{"disambiguationData":[OSD([subQ0])]})],"blendedInto":[makeQuery(id+"F12.opRevolve","SWEPT_FACE",FACE,{"disambiguationData":[OSD([subQ0])]})]});}
            var Q1;
            {var subQ0=sQuery(id+"F11.wireOp",EDGE,"E21");Q1=makeQuery(id+"F13.opChamfer","BLEND_EDGE",EDGE,{"blendedFrom":[makeQuery(id+"F12.opRevolve","SWEPT_EDGE",EDGE,{"disambiguationData":[OSD([sQuery(id+"F11.wireOp",EDGE,"E20"),subQ0])]}),makeQuery(id+"F12.opRevolve","SWEPT_FACE",FACE,{"disambiguationData":[OSD([subQ0])]})],"blendedInto":[makeQuery(id+"F12.opRevolve","SWEPT_FACE",FACE,{"disambiguationData":[OSD([subQ0])]})]});}
            fillet(context, id + "F14", {"entities" : qUnion([Q0, Q1]), "radius" : 3 * mm, "tangentPropagation" : true, "allowEdgeOverflow" : false});
        }
    });
